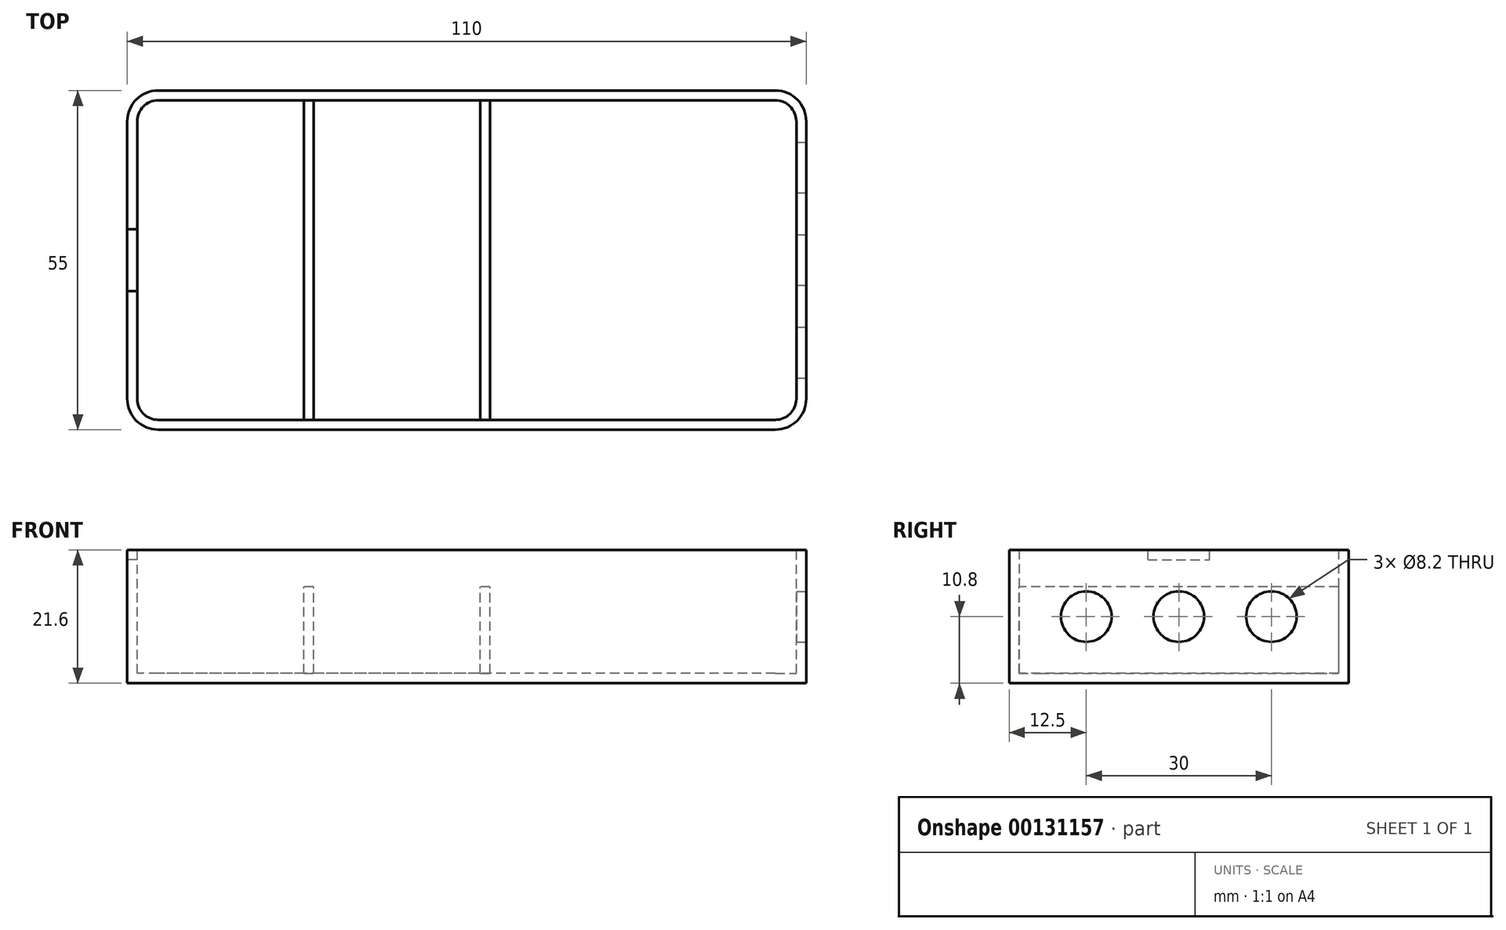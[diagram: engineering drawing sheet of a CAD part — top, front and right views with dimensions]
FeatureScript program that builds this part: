
annotation { "Feature Type Name" : "Feature", "Feature Type Description" : "" }
export const myFeature = defineFeature(function(context is Context, id is Id, definition is map)
    precondition{}
    {
        {
            var Q0;
            Q0=qCreatedBy(makeId("Top.planeOp"),FACE);
            var sketch = newSketch(context, id + "F0", { "sketchPlane" : qUnion([Q0])});
            skLineSegment(sketch, "E0.bottom", {"start": v(55, -27.5) * mm, "end": v(-55, -27.5) * mm});
            skLineSegment(sketch, "E0.top", {"start": v(55, 27.5) * mm, "end": v(-55, 27.5) * mm});
            skLineSegment(sketch, "E0.left", {"start": v(55, -27.5) * mm, "end": v(55, 27.5) * mm});
            skLineSegment(sketch, "E0.right", {"start": v(-55, -27.5) * mm, "end": v(-55, 27.5) * mm});
            skPoint(sketch, "E0.middle", {"position": v(0, 0) * mm});
            skLineSegment(sketch, "E1.bottom", {"start": v(52.5, 25) * mm, "end": v(-23.5, 25) * mm, "construction": true});
            skLineSegment(sketch, "E1.top", {"start": v(52.5, -25) * mm, "end": v(-23.5, -25) * mm, "construction": true});
            skLineSegment(sketch, "E1.left", {"start": v(52.5, 25) * mm, "end": v(52.5, -25) * mm, "construction": true});
            skLineSegment(sketch, "E1.right", {"start": v(-23.5, 25) * mm, "end": v(-23.5, -25) * mm, "construction": true});
            skSolve(sketch);
        }
        {
            var Q0;
            Q0=qSketchRegion(id+"F0",true);
            extrude(context, id + "F1", {"entities" : qUnion([Q0]), "depth" : 21.6 * mm});
        }
        {
            var Q0;
            Q0=makeQuery(id+"F1.opExtrude","SWEPT_EDGE",EDGE,{"disambiguationData":[OSD([sQuery(id+"F0.wireOp",EDGE,"E0.bottom"),sQuery(id+"F0.wireOp",EDGE,"E0.right")])]});
            var Q1;
            Q1=makeQuery(id+"F1.opExtrude","SWEPT_EDGE",EDGE,{"disambiguationData":[OSD([sQuery(id+"F0.wireOp",EDGE,"E0.bottom"),sQuery(id+"F0.wireOp",EDGE,"E0.left")])]});
            var Q2;
            Q2=makeQuery(id+"F1.opExtrude","SWEPT_EDGE",EDGE,{"disambiguationData":[OSD([sQuery(id+"F0.wireOp",EDGE,"E0.top"),sQuery(id+"F0.wireOp",EDGE,"E0.left")])]});
            var Q3;
            Q3=makeQuery(id+"F1.opExtrude","SWEPT_EDGE",EDGE,{"disambiguationData":[OSD([sQuery(id+"F0.wireOp",EDGE,"E0.top"),sQuery(id+"F0.wireOp",EDGE,"E0.right")])]});
            fillet(context, id + "F2", {"entities" : qUnion([Q0, Q1, Q2, Q3]), "radius" : 5 * mm, "tangentPropagation" : true, "allowEdgeOverflow" : false});
        }
        {
            var Q0;
            Q0=makeQuery(id+"F1.opExtrude","CAP_FACE",FACE,{"disambiguationData":[OSD([sQuery(id+"F0.wireOp",EDGE,"E0.bottom"),sQuery(id+"F0.wireOp",EDGE,"E0.top"),sQuery(id+"F0.wireOp",EDGE,"E0.left"),sQuery(id+"F0.wireOp",EDGE,"E0.right")])],"isStart":false});
            shell(context, id + "F3", {"entities" : qUnion([Q0]), "thickness" : 1.6 * mm});
        }
        {
            var Q0;
            Q0=makeQuery(id+"F3.opShell","OFFSET_FACE",FACE,{"disambiguationData":[OSD([sQuery(id+"F0.wireOp",EDGE,"E0.bottom"),sQuery(id+"F0.wireOp",EDGE,"E0.top"),sQuery(id+"F0.wireOp",EDGE,"E0.left"),sQuery(id+"F0.wireOp",EDGE,"E0.right")])]});
            var sketch = newSketch(context, id + "F4", { "sketchPlane" : qUnion([Q0])});
            skSolve(sketch);
        }
        {
            var Q0;
            {var subQ3=sQuery(id+"F0.wireOp",EDGE,"E0.bottom");Q0=makeQuery(id+"F4.imprint","IMPRINT",FACE,{"disambiguationData":[TD([[makeQuery(id+"F4.imprint","IMPRINT",EDGE,{"derivedFrom":makeQuery(id+"F3.opShell","OFFSET_EDGE",EDGE,{"disambiguationData":[OSD([subQ3]),TDD([makeQuery(id+"F1.opExtrude","CAP_EDGE",EDGE,{"disambiguationData":[OSD([subQ3])],"isStart":true})])]})}),-1.0]])]});}
            var sketch = newSketch(context, id + "F5", { "sketchPlane" : qUnion([Q0])});
            skLineSegment(sketch, "E2", {"start": v(-26.4, 37.86) * mm, "end": v(-26.4, -37.9) * mm, "construction": true});
            skLineSegment(sketch, "E3.bottom", {"start": v(-26.4, 25.87) * mm, "end": v(-24.8, 25.87) * mm});
            skLineSegment(sketch, "E3.top", {"start": v(-26.4, -25.93) * mm, "end": v(-24.8, -25.93) * mm});
            skLineSegment(sketch, "E3.left", {"start": v(-26.4, 25.87) * mm, "end": v(-26.4, -25.93) * mm});
            skLineSegment(sketch, "E3.right", {"start": v(-24.8, 25.87) * mm, "end": v(-24.8, -25.93) * mm});
            skLineSegment(sketch, "E4", {"start": v(-26.4, 25.87) * mm, "end": v(30.94, 25.87) * mm, "construction": true});
            skLineSegment(sketch, "E5", {"start": v(-24.8, -25.93) * mm, "end": v(17.93, -25.93) * mm, "construction": true});
            skLineSegment(sketch, "E6.bottom", {"start": v(2.2, 25.87) * mm, "end": v(3.8, 25.87) * mm});
            skLineSegment(sketch, "E6.top", {"start": v(2.2, -25.93) * mm, "end": v(3.8, -25.93) * mm});
            skLineSegment(sketch, "E6.left", {"start": v(2.2, 25.87) * mm, "end": v(2.2, -25.93) * mm});
            skLineSegment(sketch, "E6.right", {"start": v(3.8, 25.87) * mm, "end": v(3.8, -25.93) * mm});
            skSolve(sketch);
        }
        {
            var Q0;
            Q0=qSketchRegion(id+"F5",true);
            extrude(context, id + "F6", {"entities" : qUnion([Q0]), "operationType" : NewBodyOperationType.ADD, "depth" : 14 * mm, "offsetDistance" : 25 * mm});
        }
        {
            var Q0;
            Q0=makeQuery(id+"F1.opExtrude","SWEPT_FACE",FACE,{"disambiguationData":[OSD([sQuery(id+"F0.wireOp",EDGE,"E0.right")])]});
            var sketch = newSketch(context, id + "F7", { "sketchPlane" : qUnion([Q0])});
            skLineSegment(sketch, "E7.bottom", {"start": v(-5, 21.6) * mm, "end": v(5, 21.6) * mm});
            skLineSegment(sketch, "E7.top", {"start": v(-5, 20) * mm, "end": v(5, 20) * mm});
            skLineSegment(sketch, "E7.left", {"start": v(-5, 21.6) * mm, "end": v(-5, 20) * mm});
            skLineSegment(sketch, "E7.right", {"start": v(5, 21.6) * mm, "end": v(5, 20) * mm});
            skSolve(sketch);
        }
        {
            var Q0;
            Q0=qSketchRegion(id+"F7",true);
            extrude(context, id + "F8", {"entities" : qUnion([Q0]), "operationType" : NewBodyOperationType.REMOVE, "endBound" : BoundingType.UP_TO_NEXT, "oppositeDirection" : true, "depth" : 25 * mm});
        }
        {
            var Q0;
            Q0=makeQuery(id+"F1.opExtrude","SWEPT_FACE",FACE,{"disambiguationData":[OSD([sQuery(id+"F0.wireOp",EDGE,"E0.left")])]});
            var sketch = newSketch(context, id + "F9", { "sketchPlane" : qUnion([Q0])});
            skLineSegment(sketch, "E8", {"start": v(-22.5, 10.8) * mm, "end": v(22.5, 10.8) * mm, "construction": true});
            skLineSegment(sketch, "E9", {"start": v(0, 21.6) * mm, "end": v(0, 0) * mm, "construction": true});
            skCircle(sketch, "E10", {"center": v(0, 10.8) * mm, "radius": 4.1 * mm});
            skCircle(sketch, "E11", {"center": v(-15, 10.8) * mm, "radius": 4.1 * mm});
            skCircle(sketch, "E12.MirrorC", {"center": v(15, 10.8) * mm, "radius": 4.1 * mm});
            skSolve(sketch);
        }
        {
            var Q0;
            Q0 = qSketchRegion(id + "F9", true);
            extrude(context, id + "F10", {"entities" : qUnion([Q0]), "operationType" : NewBodyOperationType.REMOVE, "oppositeDirection" : true, "depth" : 3 * mm, "offsetDistance" : 25 * mm});
        }
    });
